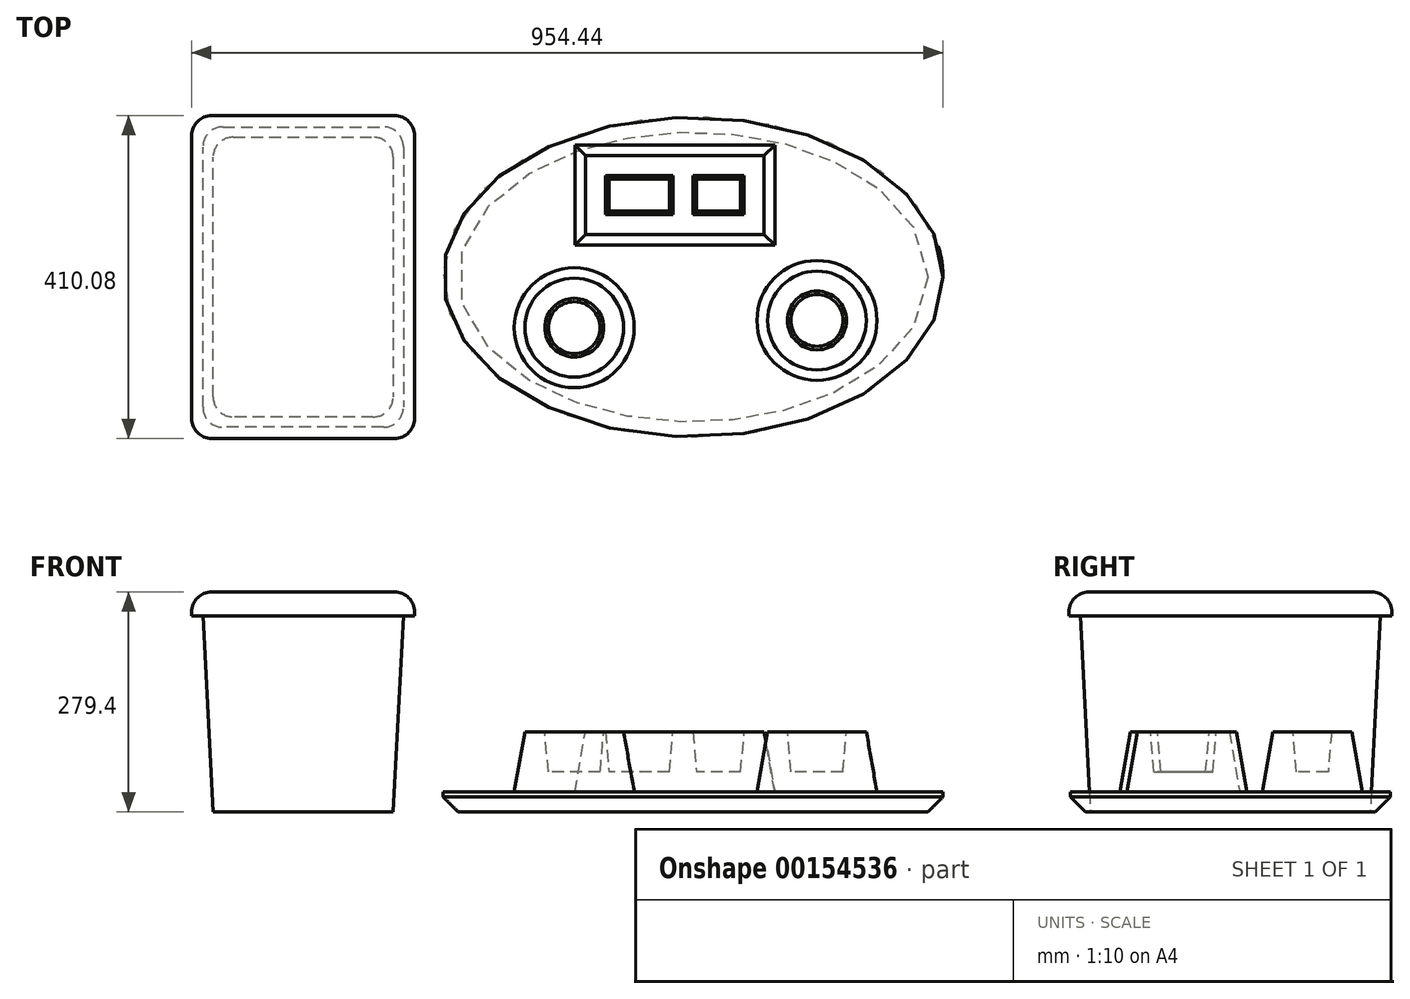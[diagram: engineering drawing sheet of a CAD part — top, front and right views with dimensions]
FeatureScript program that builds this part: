
annotation { "Feature Type Name" : "Feature", "Feature Type Description" : "" }
export const myFeature = defineFeature(function(context is Context, id is Id, definition is map)
    precondition{}
    {
        {
            var Q0;
            Q0=qCreatedBy(makeId("Top.planeOp"),FACE);
            var sketch = newSketch(context, id + "F0", { "sketchPlane" : qUnion([Q0])});
            skEllipse(sketch, "E0", {"center": v(0, 0) * mm, "majorRadius": 317.5 * mm, "minorRadius": 203.2 * mm, "majorAxis": v(1, 0)});
            skLineSegment(sketch, "E1.bottom", {"start": v(-609.6, 177.7) * mm, "end": v(-381, 177.7) * mm});
            skLineSegment(sketch, "E1.top", {"start": v(-609.6, -177.7) * mm, "end": v(-381, -177.7) * mm});
            skLineSegment(sketch, "E1.left", {"start": v(-609.6, 177.7) * mm, "end": v(-609.6, -177.7) * mm});
            skLineSegment(sketch, "E1.right", {"start": v(-381, 177.7) * mm, "end": v(-381, -177.7) * mm});
            skLineSegment(sketch, "E2", {"start": v(-609.6, 0) * mm, "end": v(-381, 0) * mm, "construction": true});
            skSolve(sketch);
        }
        {
            var Q0;
            Q0=makeQuery(id+"F0.imprint","IMPRINT",FACE,{"disambiguationData":[TD([[makeQuery(id+"F0.imprint","IMPRINT",EDGE,{"derivedFrom":sQuery(id+"F0.wireOp",EDGE,"E0")}),1.0]])]});
            extrude(context, id + "F1", {"entities" : qUnion([Q0]), "depth" : 25.4 * mm});
        }
        {
            var Q0;
            Q0=makeQuery(id+"F1.opExtrude","CAP_FACE",FACE,{"disambiguationData":[OSD([sQuery(id+"F0.wireOp",EDGE,"E0")])],"isStart":false});
            var sketch = newSketch(context, id + "F2", { "sketchPlane" : qUnion([Q0])});
            skCircle(sketch, "E3", {"center": v(157.42, -55.2) * mm, "radius": 76.2 * mm});
            skCircle(sketch, "E4", {"center": v(-150.92, -64.32) * mm, "radius": 76.2 * mm});
            skLineSegment(sketch, "E5.bottom", {"start": v(-150.2, 167.5) * mm, "end": v(103.8, 167.5) * mm});
            skLineSegment(sketch, "E5.top", {"start": v(-150.2, 40.5) * mm, "end": v(103.8, 40.5) * mm});
            skLineSegment(sketch, "E5.left", {"start": v(-150.2, 167.5) * mm, "end": v(-150.2, 40.5) * mm});
            skLineSegment(sketch, "E5.right", {"start": v(103.8, 167.5) * mm, "end": v(103.8, 40.5) * mm});
            skSolve(sketch);
        }
        {
            var Q0;
            Q0=makeQuery(id+"F2.imprint","IMPRINT",FACE,{"disambiguationData":[TD([[makeQuery(id+"F2.imprint","IMPRINT",EDGE,{"derivedFrom":sQuery(id+"F2.wireOp",EDGE,"E5.bottom")}),-1.0]])]});
            var Q1;
            Q1=makeQuery(id+"F2.imprint","IMPRINT",FACE,{"disambiguationData":[TD([[makeQuery(id+"F2.imprint","IMPRINT",EDGE,{"derivedFrom":sQuery(id+"F2.wireOp",EDGE,"E4")}),1.0]])]});
            var Q2;
            Q2=makeQuery(id+"F2.imprint","IMPRINT",FACE,{"disambiguationData":[TD([[makeQuery(id+"F2.imprint","IMPRINT",EDGE,{"derivedFrom":sQuery(id+"F2.wireOp",EDGE,"E3")}),1.0]])]});
            extrude(context, id + "F3", {"entities" : qUnion([Q0, Q1, Q2]), "operationType" : NewBodyOperationType.ADD, "depth" : 76.2 * mm, "hasDraft" : true, "draftAngle" : 10 * degree, "draftPullDirection" : true});
        }
        {
            var Q0;
            Q0=makeQuery(id+"F3.opExtrude","CAP_FACE",FACE,{"disambiguationData":[OSD([sQuery(id+"F2.wireOp",EDGE,"E5.bottom"),sQuery(id+"F2.wireOp",EDGE,"E5.top"),sQuery(id+"F2.wireOp",EDGE,"E5.left"),sQuery(id+"F2.wireOp",EDGE,"E5.right")])],"isStart":false});
            var sketch = newSketch(context, id + "F4", { "sketchPlane" : qUnion([Q0])});
            skLineSegment(sketch, "E6.bottom", {"start": v(-111.36, 128.66) * mm, "end": v(64.97, 128.66) * mm});
            skLineSegment(sketch, "E6.top", {"start": v(-111.36, 79.33) * mm, "end": v(64.97, 79.33) * mm});
            skLineSegment(sketch, "E6.left", {"start": v(-111.36, 128.66) * mm, "end": v(-111.36, 79.33) * mm});
            skLineSegment(sketch, "E6.right", {"start": v(64.97, 128.66) * mm, "end": v(64.97, 79.33) * mm});
            skCircle(sketch, "E7", {"center": v(-150.92, -64.32) * mm, "radius": 37.36 * mm});
            skCircle(sketch, "E8", {"center": v(157.42, -55.2) * mm, "radius": 37.36 * mm});
            skLineSegment(sketch, "E9", {"start": v(-25.4, 128.66) * mm, "end": v(-25.4, 79.33) * mm});
            skLineSegment(sketch, "E10", {"start": v(0, 128.66) * mm, "end": v(0, 79.33) * mm});
            skSolve(sketch);
        }
        {
            var Q0;
            {var subQ0=sQuery(id+"F4.wireOp",EDGE,"E6.left");Q0=makeQuery(id+"F4.imprint","IMPRINT",FACE,{"disambiguationData":[TD([[makeQuery(id+"F4.imprint","IMPRINT",EDGE,{"derivedFrom":subQ0}),1.0]])]});}
            var Q1;
            {var subQ0=sQuery(id+"F4.wireOp",EDGE,"E6.right");Q1=makeQuery(id+"F4.imprint","IMPRINT",FACE,{"disambiguationData":[TD([[makeQuery(id+"F4.imprint","IMPRINT",EDGE,{"derivedFrom":subQ0}),-1.0]])]});}
            var Q2;
            Q2=makeQuery(id+"F4.imprint","IMPRINT",FACE,{"disambiguationData":[TD([[makeQuery(id+"F4.imprint","IMPRINT",EDGE,{"derivedFrom":sQuery(id+"F4.wireOp",EDGE,"E8")}),1.0]])]});
            var Q3;
            Q3=makeQuery(id+"F4.imprint","IMPRINT",FACE,{"disambiguationData":[TD([[makeQuery(id+"F4.imprint","IMPRINT",EDGE,{"derivedFrom":sQuery(id+"F4.wireOp",EDGE,"E7")}),1.0]])]});
            extrude(context, id + "F5", {"entities" : qUnion([Q0, Q1, Q2, Q3]), "operationType" : NewBodyOperationType.REMOVE, "oppositeDirection" : true, "depth" : 50.8 * mm, "hasDraft" : true, "draftAngle" : 5 * degree, "draftPullDirection" : true});
        }
        {
            var Q0;
            Q0=makeQuery(id+"F0.imprint","IMPRINT",FACE,{"disambiguationData":[TD([[makeQuery(id+"F0.imprint","IMPRINT",EDGE,{"derivedFrom":sQuery(id+"F0.wireOp",EDGE,"E1.bottom")}),-1.0]])]});
            extrude(context, id + "F6", {"entities" : qUnion([Q0]), "depth" : 279.4 * mm, "hasDraft" : true, "draftAngle" : 3 * degree});
        }
        {
            var Q0;
            Q0=makeQuery(id+"F6.opExtrude","CAP_FACE",FACE,{"disambiguationData":[OSD([sQuery(id+"F0.wireOp",EDGE,"E1.bottom"),sQuery(id+"F0.wireOp",EDGE,"E1.top"),sQuery(id+"F0.wireOp",EDGE,"E1.left"),sQuery(id+"F0.wireOp",EDGE,"E1.right")])],"isStart":false});
            var sketch = newSketch(context, id + "F7", { "sketchPlane" : qUnion([Q0])});
            skLineSegment(sketch, "E11.bottom", {"start": v(-353.66, 205.04) * mm, "end": v(-636.94, 205.04) * mm});
            skLineSegment(sketch, "E11.top", {"start": v(-353.66, -205.04) * mm, "end": v(-636.94, -205.04) * mm});
            skLineSegment(sketch, "E11.left", {"start": v(-353.66, 205.04) * mm, "end": v(-353.66, -205.04) * mm});
            skLineSegment(sketch, "E11.right", {"start": v(-636.94, 205.04) * mm, "end": v(-636.94, -205.04) * mm});
            skSolve(sketch);
        }
        {
            var Q0;
            Q0=makeQuery(id+"F7.imprint","IMPRINT",FACE,{"disambiguationData":[TD([[makeQuery(id+"F7.imprint","IMPRINT",EDGE,{"derivedFrom":sQuery(id+"F7.wireOp",EDGE,"E11.bottom")}),1.0]])]});
            var Q1;
            Q1=makeQuery(id+"F7.imprint","IMPRINT",FACE,{"disambiguationData":[TD([[makeQuery(id+"F7.imprint","IMPRINT",EDGE,{"derivedFrom":makeQuery(id+"F6.opExtrude","CAP_EDGE",EDGE,{"disambiguationData":[OSD([sQuery(id+"F0.wireOp",EDGE,"E1.bottom")])],"isStart":false})}),-1.0]])]});
            extrude(context, id + "F8", {"entities" : qUnion([Q0, Q1]), "operationType" : NewBodyOperationType.ADD, "oppositeDirection" : true, "depth" : 30.48 * mm});
        }
        {
            var Q0;
            Q0=makeQuery(id+"F8.boolean.opBoolean","MERGE",FACE,{"derivedFrom":[makeQuery(id+"F6.opExtrude","CAP_FACE",FACE,{"disambiguationData":[OSD([sQuery(id+"F0.wireOp",EDGE,"E1.bottom"),sQuery(id+"F0.wireOp",EDGE,"E1.top"),sQuery(id+"F0.wireOp",EDGE,"E1.left"),sQuery(id+"F0.wireOp",EDGE,"E1.right")])],"isStart":false}),makeQuery(id+"F8.opExtrude","CAP_FACE",FACE,{"disambiguationData":[OSD([sQuery(id+"F7.wireOp",EDGE,"E11.bottom"),sQuery(id+"F7.wireOp",EDGE,"E11.top"),sQuery(id+"F7.wireOp",EDGE,"E11.left"),sQuery(id+"F7.wireOp",EDGE,"E11.right")])],"isStart":true})]});
            var Q1;
            Q1=makeQuery(id+"F8.opExtrude","SWEPT_EDGE",EDGE,{"disambiguationData":[OSD([sQuery(id+"F7.wireOp",EDGE,"E11.top"),sQuery(id+"F7.wireOp",EDGE,"E11.left")])]});
            var Q2;
            Q2=makeQuery(id+"F8.opExtrude","SWEPT_EDGE",EDGE,{"disambiguationData":[OSD([sQuery(id+"F7.wireOp",EDGE,"E11.bottom"),sQuery(id+"F7.wireOp",EDGE,"E11.left")])]});
            var Q3;
            Q3=makeQuery(id+"F8.opExtrude","SWEPT_EDGE",EDGE,{"disambiguationData":[OSD([sQuery(id+"F7.wireOp",EDGE,"E11.top"),sQuery(id+"F7.wireOp",EDGE,"E11.right")])]});
            var Q4;
            Q4=makeQuery(id+"F8.opExtrude","SWEPT_EDGE",EDGE,{"disambiguationData":[OSD([sQuery(id+"F7.wireOp",EDGE,"E11.bottom"),sQuery(id+"F7.wireOp",EDGE,"E11.right")])]});
            var Q5;
            Q5=makeQuery(id+"F6.opExtrude","SWEPT_EDGE",EDGE,{"disambiguationData":[OSD([sQuery(id+"F0.wireOp",EDGE,"E1.bottom"),sQuery(id+"F0.wireOp",EDGE,"E1.left")])]});
            var Q6;
            Q6=makeQuery(id+"F6.opExtrude","SWEPT_EDGE",EDGE,{"disambiguationData":[OSD([sQuery(id+"F0.wireOp",EDGE,"E1.bottom"),sQuery(id+"F0.wireOp",EDGE,"E1.right")])]});
            var Q7;
            Q7=makeQuery(id+"F6.opExtrude","SWEPT_EDGE",EDGE,{"disambiguationData":[OSD([sQuery(id+"F0.wireOp",EDGE,"E1.top"),sQuery(id+"F0.wireOp",EDGE,"E1.left")])]});
            var Q8;
            Q8=makeQuery(id+"F6.opExtrude","SWEPT_EDGE",EDGE,{"disambiguationData":[OSD([sQuery(id+"F0.wireOp",EDGE,"E1.top"),sQuery(id+"F0.wireOp",EDGE,"E1.right")])]});
            fillet(context, id + "F9", {"entities" : qUnion([Q0, Q1, Q2, Q3, Q4, Q5, Q6, Q7, Q8]), "radius" : 25.4 * mm, "tangentPropagation" : true, "allowEdgeOverflow" : false});
        }
        {
            var Q0;
            Q0=makeQuery(id+"F1.opExtrude","CAP_FACE",FACE,{"disambiguationData":[OSD([sQuery(id+"F0.wireOp",EDGE,"E0")])],"isStart":true});
            chamfer(context, id + "F10", {"entities" : qUnion([Q0]), "width" : 19.05 * mm, "tangentPropagation" : true});
        }
    });
